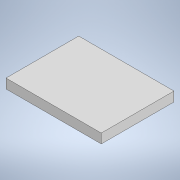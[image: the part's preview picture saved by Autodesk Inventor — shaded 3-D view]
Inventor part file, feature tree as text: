
AUTODESK INVENTOR PART (.ipt)
format: ipt  version: 2020 (Build 240168000, 168)  size: 89,088 bytes
history: native  units: in
note: dims shown in document units (in); Inventor stores cm internally (conversion verified against a paired STEP export)
features: extrude x1, sketch x1
ambient origin geometry x8: Origin, YZ Plane, XZ Plane, XY Plane, X Axis, Y Axis, Z Axis, Center Point
bodies: Solid1 (feature_tree)
feature tree (2):
  extrude  "Extrusion1"  Depth=0.961in
  sketch  "Sketch1"  dims[d0=1.259in d1=0.961in d2=0.125in d3=0.0in]
